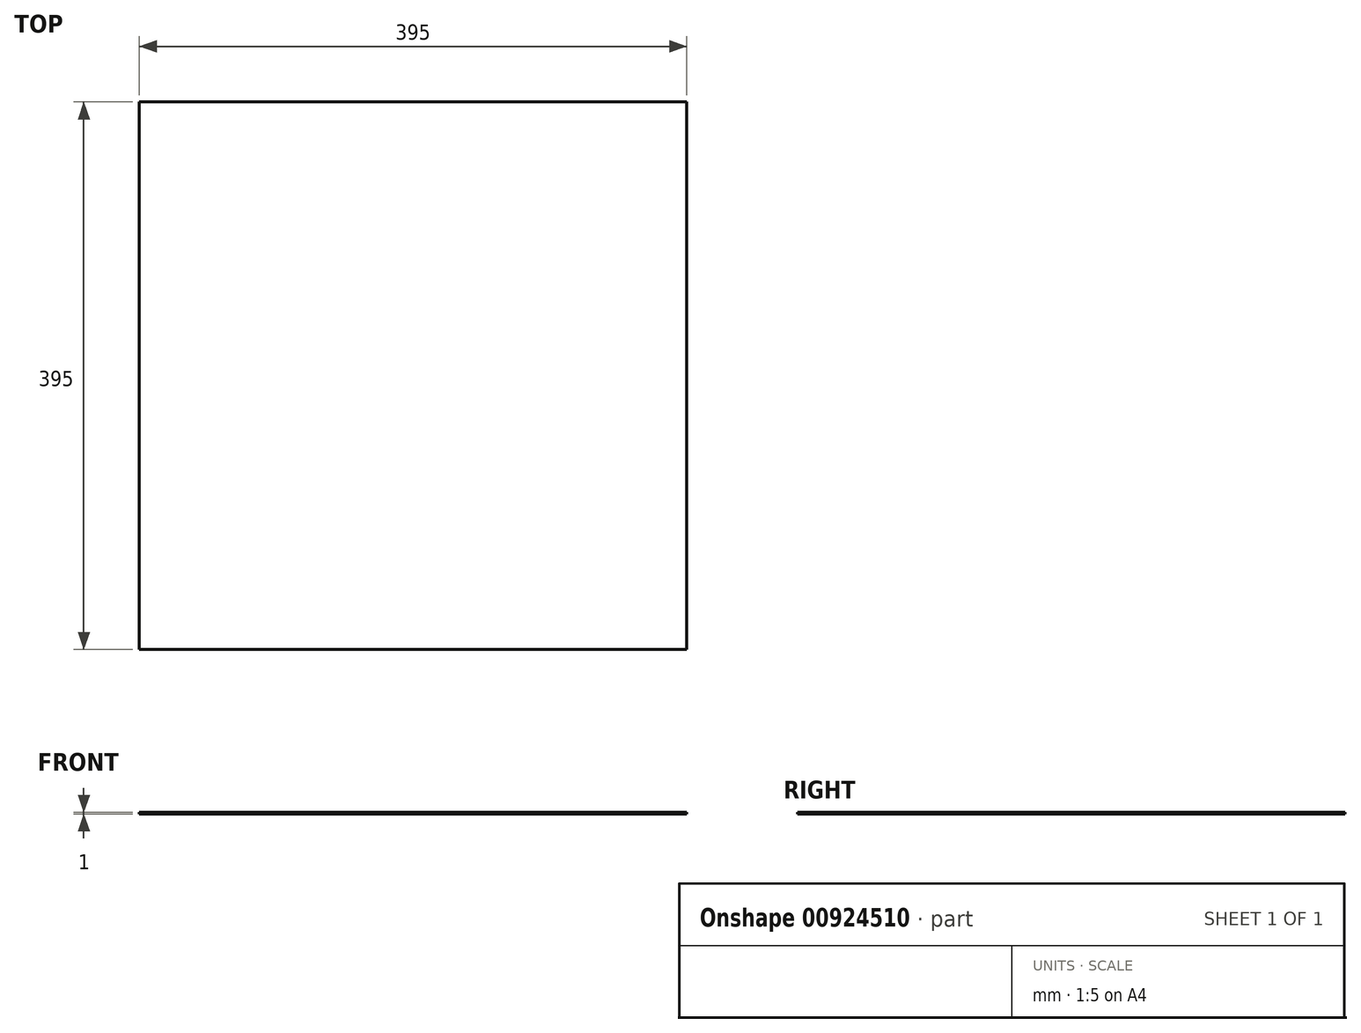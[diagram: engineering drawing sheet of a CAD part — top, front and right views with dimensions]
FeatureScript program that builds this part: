
annotation { "Feature Type Name" : "Feature", "Feature Type Description" : "" }
export const myFeature = defineFeature(function(context is Context, id is Id, definition is map)
    precondition{}
    {
        {
            var Q0;
            Q0=qCreatedBy(makeId("Top.planeOp"),FACE);
            var sketch = newSketch(context, id + "F0", { "sketchPlane" : qUnion([Q0])});
            skLineSegment(sketch, "E0.bottom", {"start": v(-197.5, 197.5) * mm, "end": v(197.5, 197.5) * mm});
            skLineSegment(sketch, "E0.top", {"start": v(-197.5, -197.5) * mm, "end": v(197.5, -197.5) * mm});
            skLineSegment(sketch, "E0.left", {"start": v(-197.5, 197.5) * mm, "end": v(-197.5, -197.5) * mm});
            skLineSegment(sketch, "E0.right", {"start": v(197.5, 197.5) * mm, "end": v(197.5, -197.5) * mm});
            skPoint(sketch, "E0.middle", {"position": v(0, 0) * mm});
            skSolve(sketch);
        }
        {
            var Q0;
            Q0=qSketchRegion(id+"F0",true);
            extrude(context, id + "F1", {"entities" : qUnion([Q0]), "depth" : 1 * mm, "offsetDistance" : 25 * mm});
        }
        {
            var Q0;
            Q0=makeQuery(id+"F1.opExtrude","SWEPT_FACE",FACE,{"disambiguationData":[OSD([sQuery(id+"F0.wireOp",EDGE,"E0.top")])]});
            var sketch = newSketch(context, id + "F2", { "sketchPlane" : qUnion([Q0])});
            skLineSegment(sketch, "E1", {"start": v(197.5, 0) * mm, "end": v(197.23, 1) * mm});
            skLineSegment(sketch, "E2", {"start": v(197.23, 1) * mm, "end": v(197.5, 1) * mm});
            skLineSegment(sketch, "E3", {"start": v(197.5, 1) * mm, "end": v(197.5, 0) * mm});
            skSolve(sketch);
        }
        {
            var Q0;
            Q0=makeQuery(id+"F2.imprint","IMPRINT",FACE,{"disambiguationData":[TD([[makeQuery(id+"F2.imprint","IMPRINT",EDGE,{"derivedFrom":sQuery(id+"F2.wireOp",EDGE,"E1")}),-1.0]])]});
            extrude(context, id + "F3", {"entities" : qUnion([Q0]), "operationType" : NewBodyOperationType.REMOVE, "oppositeDirection" : true, "depth" : 10000 * mm, "offsetDistance" : 25 * mm});
        }
    });
